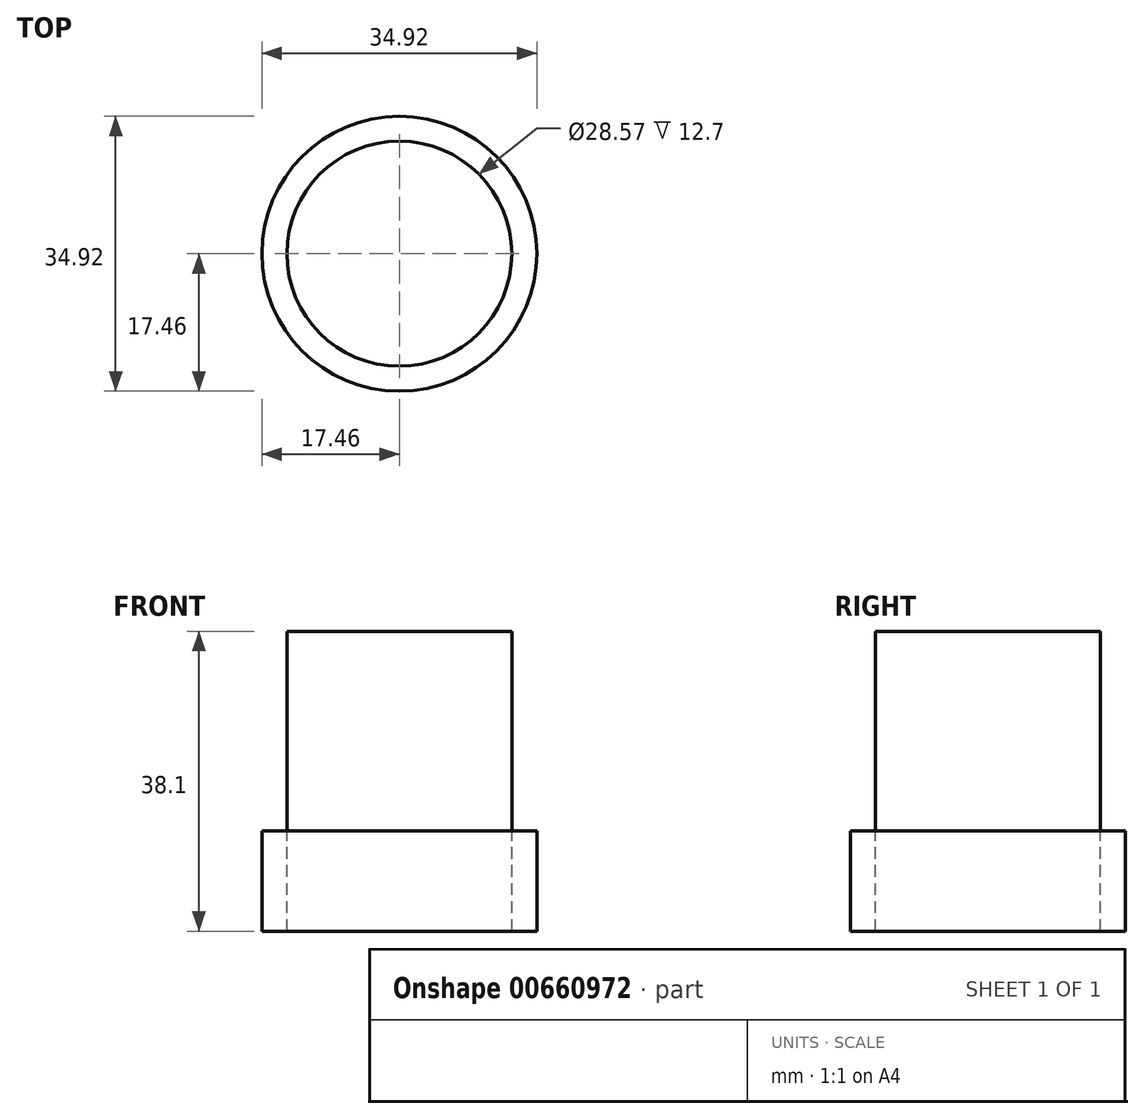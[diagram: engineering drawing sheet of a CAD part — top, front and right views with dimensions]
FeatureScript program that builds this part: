
annotation { "Feature Type Name" : "Feature", "Feature Type Description" : "" }
export const myFeature = defineFeature(function(context is Context, id is Id, definition is map)
    precondition{}
    {
        {
            var Q0;
            Q0=qCreatedBy(makeId("Top.planeOp"),FACE);
            var sketch = newSketch(context, id + "F0", { "sketchPlane" : qUnion([Q0])});
            skCircle(sketch, "E0", {"center": v(0, 0) * mm, "radius": 14.29 * mm});
            skCircle(sketch, "E1.0", {"center": v(0, 0) * mm, "radius": 17.46 * mm});
            skSolve(sketch);
        }
        {
            var Q0;
            Q0=makeQuery(id+"F0.imprint","IMPRINT",FACE,{"disambiguationData":[TD([[makeQuery(id+"F0.imprint","IMPRINT",EDGE,{"derivedFrom":sQuery(id+"F0.wireOp",EDGE,"E0")}),1.0]])]});
            extrude(context, id + "F1", {"entities" : qUnion([Q0]), "depth" : 25.4 * mm, "offsetDistance" : 25.4 * mm});
        }
        {
            var Q0;
            Q0 = qSketchRegion(id + "F0", true);
            extrude(context, id + "F2", {"entities" : qUnion([Q0]), "operationType" : NewBodyOperationType.ADD, "oppositeDirection" : true, "depth" : 12.7 * mm, "offsetDistance" : 25.4 * mm, "hasSecondDirection" : true, "secondDirectionOppositeDirection" : false, "secondDirectionDepth" : 0.03 * mm});
        }
    });
